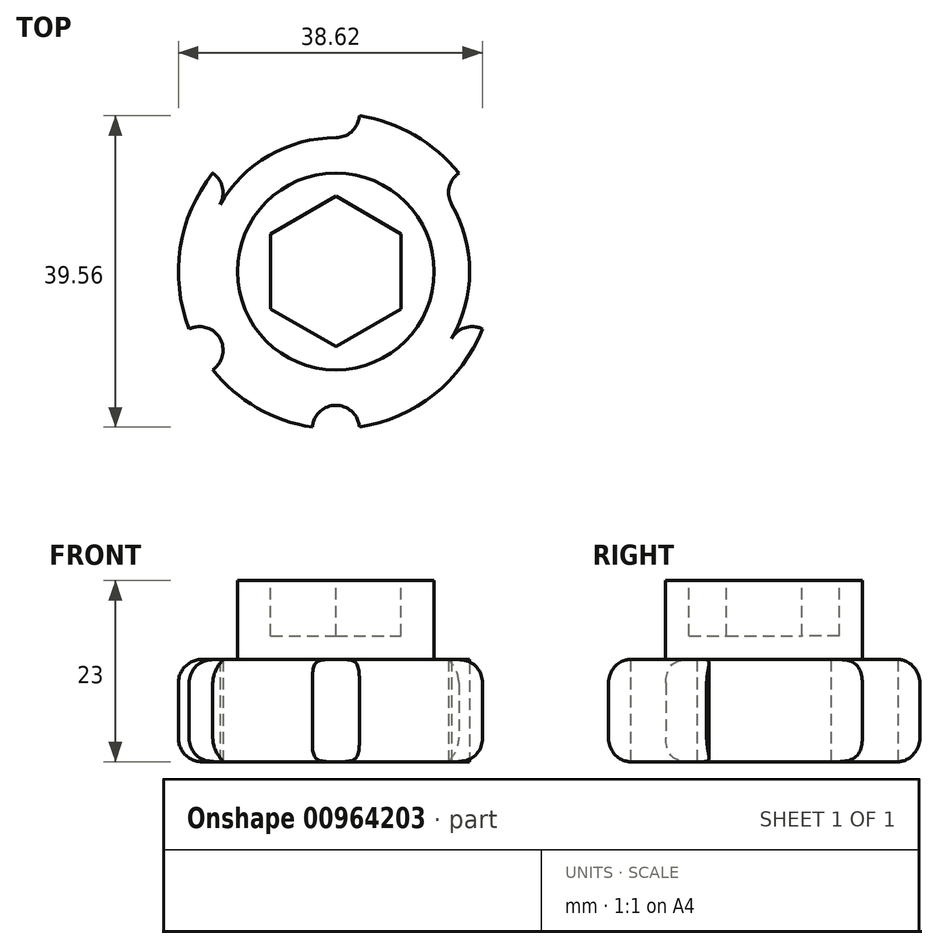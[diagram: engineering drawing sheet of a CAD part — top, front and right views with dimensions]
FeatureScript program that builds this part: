
annotation { "Feature Type Name" : "Feature", "Feature Type Description" : "" }
export const myFeature = defineFeature(function(context is Context, id is Id, definition is map)
    precondition{}
    {
        {
            var Q0;
            Q0=qCreatedBy(makeId("Top.planeOp"),FACE);
            var sketch = newSketch(context, id + "F0", { "sketchPlane" : qUnion([Q0])});
            skCircle(sketch, "E0", {"center": v(0, 0) * mm, "radius": 20 * mm});
            skSolve(sketch);
        }
        {
            var Q0;
            Q0=qSketchRegion(id+"F0",true);
            extrude(context, id + "F1", {"entities" : qUnion([Q0]), "depth" : 13 * mm, "offsetDistance" : 25 * mm});
        }
        {
            var Q0;
            Q0=makeQuery(id+"F1.opExtrude","CAP_FACE",FACE,{"disambiguationData":[OSD([sQuery(id+"F0.wireOp",EDGE,"E0")])],"isStart":false});
            var sketch = newSketch(context, id + "F2", { "sketchPlane" : qUnion([Q0])});
            skCircle(sketch, "E1", {"center": v(0, 0) * mm, "radius": 12.5 * mm});
            skSolve(sketch);
        }
        {
            var Q0;
            Q0=qSketchRegion(id+"F2",true);
            extrude(context, id + "F3", {"entities" : qUnion([Q0]), "operationType" : NewBodyOperationType.ADD, "depth" : 10 * mm, "offsetDistance" : 25 * mm});
        }
        {
            var Q0;
            Q0=makeQuery(id+"F1.opExtrude","CAP_EDGE",EDGE,{"disambiguationData":[OSD([sQuery(id+"F0.wireOp",EDGE,"E0")])],"isStart":false});
            var Q1;
            Q1=makeQuery(id+"F1.opExtrude","CAP_EDGE",EDGE,{"disambiguationData":[OSD([sQuery(id+"F0.wireOp",EDGE,"E0")])],"isStart":true});
            fillet(context, id + "F4", {"entities" : qUnion([Q0, Q1]), "radius" : 3 * mm, "tangentPropagation" : true, "allowEdgeOverflow" : false});
        }
        {
            var Q0;
            Q0=makeQuery(id+"F3.opExtrude","CAP_FACE",FACE,{"disambiguationData":[OSD([sQuery(id+"F2.wireOp",EDGE,"E1")])],"isStart":false});
            var sketch = newSketch(context, id + "F5", { "sketchPlane" : qUnion([Q0])});
            skCircle(sketch, "E2.cCircle", {"center": v(0, 0) * mm, "radius": 9.55 * mm, "construction": true});
            skLineSegment(sketch, "E2.0", {"start": v(0, 9.55) * mm, "end": v(8.27, 4.78) * mm});
            skLineSegment(sketch, "E2.1", {"start": v(8.27, 4.78) * mm, "end": v(8.27, -4.77) * mm});
            skLineSegment(sketch, "E2.2", {"start": v(8.27, -4.77) * mm, "end": v(0, -9.55) * mm});
            skLineSegment(sketch, "E2.3", {"start": v(0, -9.55) * mm, "end": v(-8.27, -4.78) * mm});
            skLineSegment(sketch, "E2.4", {"start": v(-8.27, -4.78) * mm, "end": v(-8.27, 4.77) * mm});
            skLineSegment(sketch, "E2.5", {"start": v(-8.27, 4.77) * mm, "end": v(0, 9.55) * mm});
            skSolve(sketch);
        }
        {
            var Q0;
            Q0=makeQuery(id+"F5.imprint","IMPRINT",FACE,{"disambiguationData":[TD([[makeQuery(id+"F5.imprint","IMPRINT",EDGE,{"derivedFrom":sQuery(id+"F5.wireOp",EDGE,"E2.0")}),-1.0]])]});
            extrude(context, id + "F6", {"entities" : qUnion([Q0]), "operationType" : NewBodyOperationType.REMOVE, "oppositeDirection" : true, "depth" : 7 * mm, "offsetDistance" : 25 * mm});
        }
        {
            var Q0;
            Q0=makeQuery(id+"F1.opExtrude","CAP_FACE",FACE,{"disambiguationData":[OSD([sQuery(id+"F0.wireOp",EDGE,"E0")])],"isStart":true});
            var sketch = newSketch(context, id + "F7", { "sketchPlane" : qUnion([Q0])});
            skCircle(sketch, "E3.0", {"center": v(0, 0) * mm, "radius": 20 * mm});
            skCircle(sketch, "E4", {"center": v(0, 20) * mm, "radius": 3 * mm});
            skCircle(sketch, "E5.1.0", {"center": v(-17.32, 10) * mm, "radius": 3 * mm});
            skCircle(sketch, "E5.2.0", {"center": v(-17.32, -10) * mm, "radius": 3 * mm});
            skCircle(sketch, "E5.3.0", {"center": v(0, -20) * mm, "radius": 3 * mm});
            skCircle(sketch, "E5.4.0", {"center": v(17.32, -10) * mm, "radius": 3 * mm});
            skCircle(sketch, "E5.5.0", {"center": v(17.32, 10) * mm, "radius": 3 * mm});
            skSolve(sketch);
        }
        {
            var Q0;
            {var subQ0=sQuery(id+"F7.wireOp",EDGE,"E5.1.0");var subQ1=sQuery(id+"F7.wireOp",EDGE,"E3.0");var subQ2=makeQuery(id+"F7.imprint","INTERSECT",VERTEX,{"disambiguationData":[OD(0.0)],"derivedFrom":[subQ1,subQ0]});Q0=makeQuery(id+"F7.imprint","IMPRINT",FACE,{"disambiguationData":[TD([[makeQuery(id+"F7.imprint","IMPRINT",EDGE,{"disambiguationData":[TD([[subQ2,-1.0]])],"derivedFrom":subQ1}),1.0]])]});}
            var Q1;
            {var subQ0=sQuery(id+"F7.wireOp",EDGE,"E4");var subQ1=sQuery(id+"F7.wireOp",EDGE,"E3.0");var subQ2=makeQuery(id+"F7.imprint","INTERSECT",VERTEX,{"disambiguationData":[OD(0.0)],"derivedFrom":[subQ1,subQ0]});Q1=makeQuery(id+"F7.imprint","IMPRINT",FACE,{"disambiguationData":[TD([[makeQuery(id+"F7.imprint","IMPRINT",EDGE,{"disambiguationData":[TD([[subQ2,-1.0]])],"derivedFrom":subQ1}),1.0]])]});}
            var Q2;
            {var subQ0=sQuery(id+"F7.wireOp",EDGE,"E4");var subQ1=sQuery(id+"F7.wireOp",EDGE,"E3.0");var subQ2=makeQuery(id+"F7.imprint","INTERSECT",VERTEX,{"disambiguationData":[OD(0.0)],"derivedFrom":[subQ1,subQ0]});Q2=makeQuery(id+"F7.imprint","IMPRINT",FACE,{"disambiguationData":[TD([[makeQuery(id+"F7.imprint","IMPRINT",EDGE,{"disambiguationData":[TD([[subQ2,-1.0]])],"derivedFrom":subQ1}),-1.0]])]});}
            var Q3;
            {var subQ0=sQuery(id+"F7.wireOp",EDGE,"E5.1.0");var subQ1=sQuery(id+"F7.wireOp",EDGE,"E3.0");var subQ2=makeQuery(id+"F7.imprint","INTERSECT",VERTEX,{"disambiguationData":[OD(0.0)],"derivedFrom":[subQ1,subQ0]});Q3=makeQuery(id+"F7.imprint","IMPRINT",FACE,{"disambiguationData":[TD([[makeQuery(id+"F7.imprint","IMPRINT",EDGE,{"disambiguationData":[TD([[subQ2,-1.0]])],"derivedFrom":subQ1}),-1.0]])]});}
            var Q4;
            {var subQ0=sQuery(id+"F7.wireOp",EDGE,"E5.2.0");var subQ1=sQuery(id+"F7.wireOp",EDGE,"E3.0");var subQ2=makeQuery(id+"F7.imprint","INTERSECT",VERTEX,{"disambiguationData":[OD(0.0)],"derivedFrom":[subQ1,subQ0]});Q4=makeQuery(id+"F7.imprint","IMPRINT",FACE,{"disambiguationData":[TD([[makeQuery(id+"F7.imprint","IMPRINT",EDGE,{"disambiguationData":[TD([[subQ2,-1.0]])],"derivedFrom":subQ1}),1.0]])]});}
            var Q5;
            {var subQ0=sQuery(id+"F7.wireOp",EDGE,"E5.2.0");var subQ1=sQuery(id+"F7.wireOp",EDGE,"E3.0");var subQ2=makeQuery(id+"F7.imprint","INTERSECT",VERTEX,{"disambiguationData":[OD(0.0)],"derivedFrom":[subQ1,subQ0]});Q5=makeQuery(id+"F7.imprint","IMPRINT",FACE,{"disambiguationData":[TD([[makeQuery(id+"F7.imprint","IMPRINT",EDGE,{"disambiguationData":[TD([[subQ2,-1.0]])],"derivedFrom":subQ1}),-1.0]])]});}
            var Q6;
            {var subQ0=sQuery(id+"F7.wireOp",EDGE,"E5.3.0");var subQ1=sQuery(id+"F7.wireOp",EDGE,"E3.0");var subQ2=makeQuery(id+"F7.imprint","INTERSECT",VERTEX,{"disambiguationData":[OD(0.0)],"derivedFrom":[subQ1,subQ0]});Q6=makeQuery(id+"F7.imprint","IMPRINT",FACE,{"disambiguationData":[TD([[makeQuery(id+"F7.imprint","IMPRINT",EDGE,{"disambiguationData":[TD([[subQ2,-1.0]])],"derivedFrom":subQ1}),1.0]])]});}
            var Q7;
            {var subQ0=sQuery(id+"F7.wireOp",EDGE,"E5.3.0");var subQ1=sQuery(id+"F7.wireOp",EDGE,"E3.0");var subQ2=makeQuery(id+"F7.imprint","INTERSECT",VERTEX,{"disambiguationData":[OD(0.0)],"derivedFrom":[subQ1,subQ0]});Q7=makeQuery(id+"F7.imprint","IMPRINT",FACE,{"disambiguationData":[TD([[makeQuery(id+"F7.imprint","IMPRINT",EDGE,{"disambiguationData":[TD([[subQ2,-1.0]])],"derivedFrom":subQ1}),-1.0]])]});}
            var Q8;
            {var subQ0=sQuery(id+"F7.wireOp",EDGE,"E5.4.0");var subQ1=sQuery(id+"F7.wireOp",EDGE,"E3.0");var subQ2=makeQuery(id+"F7.imprint","INTERSECT",VERTEX,{"disambiguationData":[OD(0.0)],"derivedFrom":[subQ1,subQ0]});Q8=makeQuery(id+"F7.imprint","IMPRINT",FACE,{"disambiguationData":[TD([[makeQuery(id+"F7.imprint","IMPRINT",EDGE,{"disambiguationData":[TD([[subQ2,-1.0]])],"derivedFrom":subQ1}),1.0]])]});}
            var Q9;
            {var subQ0=sQuery(id+"F7.wireOp",EDGE,"E5.4.0");var subQ1=sQuery(id+"F7.wireOp",EDGE,"E3.0");var subQ2=makeQuery(id+"F7.imprint","INTERSECT",VERTEX,{"disambiguationData":[OD(0.0)],"derivedFrom":[subQ1,subQ0]});Q9=makeQuery(id+"F7.imprint","IMPRINT",FACE,{"disambiguationData":[TD([[makeQuery(id+"F7.imprint","IMPRINT",EDGE,{"disambiguationData":[TD([[subQ2,-1.0]])],"derivedFrom":subQ1}),-1.0]])]});}
            var Q10;
            {var subQ0=sQuery(id+"F7.wireOp",EDGE,"E5.5.0");var subQ1=sQuery(id+"F7.wireOp",EDGE,"E3.0");var subQ2=makeQuery(id+"F7.imprint","INTERSECT",VERTEX,{"disambiguationData":[OD(0.0)],"derivedFrom":[subQ1,subQ0]});Q10=makeQuery(id+"F7.imprint","IMPRINT",FACE,{"disambiguationData":[TD([[makeQuery(id+"F7.imprint","IMPRINT",EDGE,{"disambiguationData":[TD([[subQ2,1.0]])],"derivedFrom":subQ1}),1.0]])]});}
            var Q11;
            {var subQ0=sQuery(id+"F7.wireOp",EDGE,"E5.5.0");var subQ1=sQuery(id+"F7.wireOp",EDGE,"E3.0");var subQ2=makeQuery(id+"F7.imprint","INTERSECT",VERTEX,{"disambiguationData":[OD(0.0)],"derivedFrom":[subQ1,subQ0]});Q11=makeQuery(id+"F7.imprint","IMPRINT",FACE,{"disambiguationData":[TD([[makeQuery(id+"F7.imprint","IMPRINT",EDGE,{"disambiguationData":[TD([[subQ2,1.0]])],"derivedFrom":subQ1}),-1.0]])]});}
            extrude(context, id + "F8", {"entities" : qUnion([Q0, Q1, Q2, Q3, Q4, Q5, Q6, Q7, Q8, Q9, Q10, Q11]), "operationType" : NewBodyOperationType.REMOVE, "oppositeDirection" : true, "depth" : 25 * mm, "offsetDistance" : 25 * mm});
        }
    });
